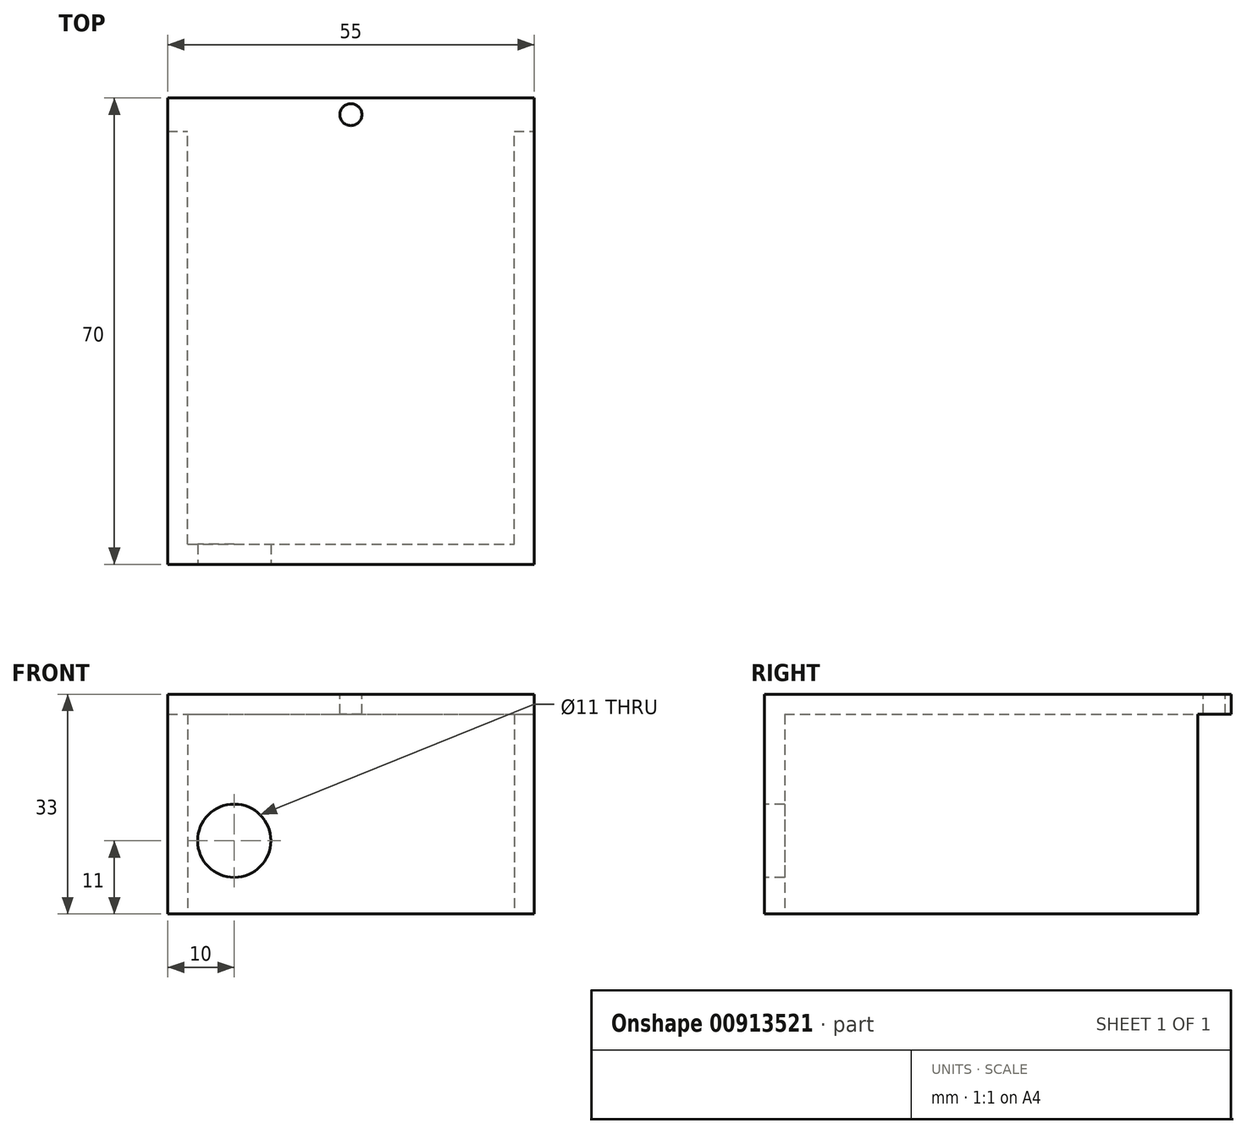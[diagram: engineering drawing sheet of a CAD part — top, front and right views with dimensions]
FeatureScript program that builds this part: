
annotation { "Feature Type Name" : "Feature", "Feature Type Description" : "" }
export const myFeature = defineFeature(function(context is Context, id is Id, definition is map)
    precondition{}
    {
        {
            var Q0;
            Q0=qCreatedBy(makeId("Top.planeOp"),FACE);
            var sketch = newSketch(context, id + "F0", { "sketchPlane" : qUnion([Q0])});
            skLineSegment(sketch, "E0.bottom", {"start": v(0, 0) * mm, "end": v(55, 0) * mm});
            skLineSegment(sketch, "E0.top", {"start": v(0, 70) * mm, "end": v(55, 70) * mm});
            skLineSegment(sketch, "E0.left", {"start": v(0, 0) * mm, "end": v(0, 70) * mm});
            skLineSegment(sketch, "E0.right", {"start": v(55, 0) * mm, "end": v(55, 70) * mm});
            skSolve(sketch);
        }
        {
            var Q0;
            Q0 = qSketchRegion(id + "F0", true);
            extrude(context, id + "F1", {"entities" : qUnion([Q0]), "depth" : 33 * mm, "offsetDistance" : 25 * mm});
        }
        {
            var Q0;
            Q0=makeQuery(id+"F1.opExtrude","CAP_FACE",FACE,{"disambiguationData":[OSD([sQuery(id+"F0.wireOp",EDGE,"E0.bottom"),sQuery(id+"F0.wireOp",EDGE,"E0.top"),sQuery(id+"F0.wireOp",EDGE,"E0.left"),sQuery(id+"F0.wireOp",EDGE,"E0.right")])],"isStart":true});
            shell(context, id + "F2", {"entities" : qUnion([Q0]), "thickness" : 3 * mm});
        }
        {
            var Q0;
            Q0=makeQuery(id+"F1.opExtrude","SWEPT_FACE",FACE,{"disambiguationData":[OSD([sQuery(id+"F0.wireOp",EDGE,"E0.right")])]});
            var sketch = newSketch(context, id + "F3", { "sketchPlane" : qUnion([Q0])});
            skLineSegment(sketch, "E1.bottom", {"start": v(65, 0) * mm, "end": v(70, 0) * mm});
            skLineSegment(sketch, "E1.top", {"start": v(65, 30) * mm, "end": v(70, 30) * mm});
            skLineSegment(sketch, "E1.left", {"start": v(65, 0) * mm, "end": v(65, 30) * mm});
            skLineSegment(sketch, "E1.right", {"start": v(70, 0) * mm, "end": v(70, 30) * mm});
            skSolve(sketch);
        }
        {
            var Q0;
            Q0 = qSketchRegion(id + "F3", true);
            extrude(context, id + "F4", {"entities" : qUnion([Q0]), "operationType" : NewBodyOperationType.REMOVE, "endBound" : BoundingType.UP_TO_NEXT, "oppositeDirection" : true, "depth" : 25 * mm, "offsetDistance" : 25 * mm});
        }
        {
            var Q0;
            Q0=makeQuery(id+"F1.opExtrude","SWEPT_FACE",FACE,{"disambiguationData":[OSD([sQuery(id+"F0.wireOp",EDGE,"E0.bottom")])]});
            var sketch = newSketch(context, id + "F5", { "sketchPlane" : qUnion([Q0])});
            skCircle(sketch, "E2", {"center": v(10, 11) * mm, "radius": 5.5 * mm});
            skSolve(sketch);
        }
        {
            var Q0;
            Q0 = qSketchRegion(id + "F5", true);
            extrude(context, id + "F6", {"entities" : qUnion([Q0]), "operationType" : NewBodyOperationType.REMOVE, "endBound" : BoundingType.UP_TO_NEXT, "oppositeDirection" : true, "depth" : 25 * mm, "offsetDistance" : 25 * mm});
        }
        {
            var Q0;
            Q0=makeQuery(id+"F1.opExtrude","CAP_FACE",FACE,{"disambiguationData":[OSD([sQuery(id+"F0.wireOp",EDGE,"E0.bottom"),sQuery(id+"F0.wireOp",EDGE,"E0.top"),sQuery(id+"F0.wireOp",EDGE,"E0.left"),sQuery(id+"F0.wireOp",EDGE,"E0.right")])],"isStart":false});
            var sketch = newSketch(context, id + "F7", { "sketchPlane" : qUnion([Q0])});
            skCircle(sketch, "E3", {"center": v(27.5, 67.5) * mm, "radius": 1.65 * mm});
            skLineSegment(sketch, "E4", {"start": v(27.5, 70) * mm, "end": v(27.5, 67.5) * mm, "construction": true});
            skSolve(sketch);
        }
        {
            var Q0;
            Q0 = qSketchRegion(id + "F7", true);
            extrude(context, id + "F8", {"entities" : qUnion([Q0]), "operationType" : NewBodyOperationType.REMOVE, "endBound" : BoundingType.UP_TO_NEXT, "oppositeDirection" : true, "depth" : 25 * mm, "offsetDistance" : 25 * mm});
        }
    });
